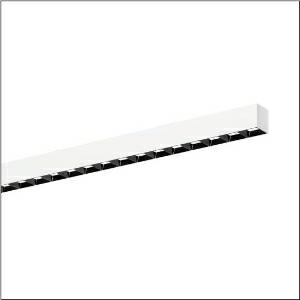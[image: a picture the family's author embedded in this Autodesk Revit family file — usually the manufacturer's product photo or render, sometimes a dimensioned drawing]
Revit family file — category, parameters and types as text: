
# Revit family: silica_r__21_51mx24da44wb_4eb4
name_source: partatom
category: Lighting Fixtures
units: mm (PartAtom-declared; Revit-internal decimal feet)

## family parameters
Cut with Voids When Loaded = No
Host = Face
Light Source = No
Part Type = Normal
Room Calculation Point = No
Round Connector Dimension = Use Diameter
Shared = No

## types (1)
- --- (1 x LED, 4320 lm, 30 W, 4000K)
    Apparent Load = 30 VA
    CIE Flux Codes = 74 94 99 100 100
    Color Rendering = 80
    Color Temperature = 4000K
    Default Elevation = 1800 mm
    Description = Silica® 21, office luminaire, primary light control with darklight reflector, of PMMA, black, CAT 2 (L<= 3000cd/m²), light emission: direct distribution, primary light characteristic: asymmetric, installation type: surface-mounted, LED, rated luminous flux: 4.320lm, luminous efficacy: 144lm/W, light colour: 840, colour temperature: 4000K, control gear: DALI 2, with terminal, 3+2-pole, max. 2.5mm², mains connection: 220..240V, AC, 50/60Hz, rated input power: 30W, luminaire housing, of aluminium, traffic white (RAL 9016), length: 1.204mm, width: 53mm, height: 53mm, protection rating (complete): IP20, insulation class (complete): insulation class I (protective earthing), certification: CE, permissible operating ambient temperature: 0..+35°C, standard: EN 50419, packaging unit: 1 piece
    Height = 53 mm
    Lamp = 1 x LED
    Lamp Light Flux = 4320 lm
    Lamp Power = 30 W
    Lamp count = 1
    Length = 1204 mm
    Luminous efficacy = 144 lm/W
    Manufacturer = Siteco
    ModVariant = No
    Model = 51MX24DA44WB
    Mounting Place = Ceiling
    Mounting Type = Surface mounted
    Number of Poles = 1
    OnlyDefault = Yes
    Power Factor = 1
    Product Name = Silica® 21
    Product group = office luminaire | ceiling mounted
    ProductGroupID = 303
    Protection Class = Protection class I
    Protection Degree = IP 20
    RLX_Detail_Level = 1
    RLX_Emergency_Light_Flux = 0 lm
    RLX_Emergency_Type = 0
    RLX_Emergency_Type_DB = No
    RlxData = <blob elided: 41729 chars, md5=1cfbc08e>
    Socket = socket
    Standby Power = 0 W
    System Light Flux = 4320 lm
    System Power = 30 W
    Type Comments = factory setting: luminous flux: 100 % | dim-lin: 254 | 418 mA
    Type Image = l_1335873.jpg
    URL = http://relux.com
    VarID = @adj_144807
    Voltage = 0 V
    Weight = 0.00 kg
    Width = 53 mm

## geometry (parser evidence)
native form markers: Blend x4, Sweep x11
no freeform markers — native parametric forms only
